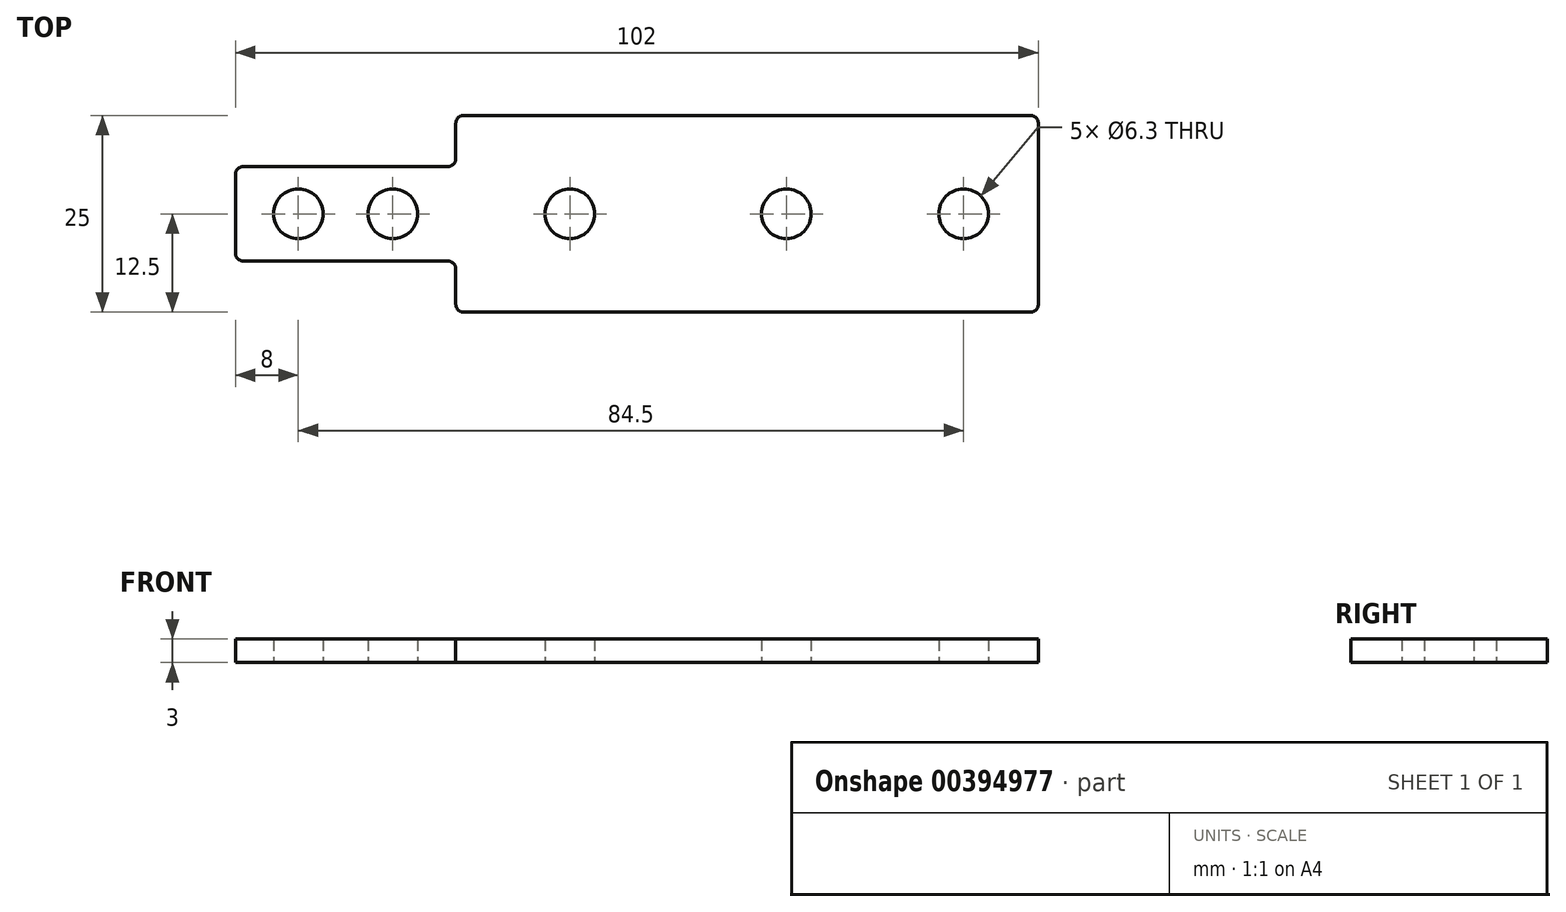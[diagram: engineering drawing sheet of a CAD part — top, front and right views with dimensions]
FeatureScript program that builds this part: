
annotation { "Feature Type Name" : "Feature", "Feature Type Description" : "" }
export const myFeature = defineFeature(function(context is Context, id is Id, definition is map)
    precondition{}
    {
        {
            var Q0;
            Q0=qCreatedBy(makeId("Top.planeOp"),FACE);
            var sketch = newSketch(context, id + "F0", { "sketchPlane" : qUnion([Q0])});
            skLineSegment(sketch, "E0.bottom", {"start": v(0, 12.5) * mm, "end": v(74, 12.5) * mm});
            skLineSegment(sketch, "E0.top", {"start": v(0, -12.5) * mm, "end": v(74, -12.5) * mm});
            skLineSegment(sketch, "E0.left", {"start": v(0, 12.5) * mm, "end": v(0, -12.5) * mm});
            skLineSegment(sketch, "E0.right", {"start": v(74, 12.5) * mm, "end": v(74, -12.5) * mm});
            skLineSegment(sketch, "E1.bottom", {"start": v(0, 6) * mm, "end": v(-28, 6) * mm});
            skLineSegment(sketch, "E1.top", {"start": v(0, -6) * mm, "end": v(-28, -6) * mm});
            skLineSegment(sketch, "E1.left", {"start": v(0, 6) * mm, "end": v(0, -6) * mm});
            skLineSegment(sketch, "E1.right", {"start": v(-28, 6) * mm, "end": v(-28, -6) * mm});
            skLineSegment(sketch, "E2", {"start": v(-28, 0) * mm, "end": v(74, 0) * mm, "construction": true});
            skCircle(sketch, "E3", {"center": v(14.5, 0) * mm, "radius": 3.15 * mm});
            skCircle(sketch, "E4", {"center": v(42, 0) * mm, "radius": 3.15 * mm});
            skCircle(sketch, "E5", {"center": v(64.5, 0) * mm, "radius": 3.15 * mm});
            skCircle(sketch, "E6", {"center": v(-20, 0) * mm, "radius": 3.15 * mm});
            skCircle(sketch, "E7", {"center": v(-8, 0) * mm, "radius": 3.15 * mm});
            skSolve(sketch);
        }
        {
            var Q0;
            Q0 = qSketchRegion(id + "F0", true);
            extrude(context, id + "F1", {"entities" : qUnion([Q0]), "depth" : 3 * mm});
        }
        {
            var Q0;
            Q0=makeQuery(id+"F1.opExtrude","SWEPT_EDGE",EDGE,{"disambiguationData":[OSD([sQuery(id+"F0.wireOp",EDGE,"E1.bottom"),sQuery(id+"F0.wireOp",EDGE,"E1.right")])]});
            var Q1;
            Q1=makeQuery(id+"F1.opExtrude","SWEPT_EDGE",EDGE,{"disambiguationData":[OSD([sQuery(id+"F0.wireOp",EDGE,"E1.top"),sQuery(id+"F0.wireOp",EDGE,"E1.right")])]});
            var Q2;
            Q2=makeQuery(id+"F1.opExtrude","SWEPT_EDGE",EDGE,{"disambiguationData":[OSD([sQuery(id+"F0.wireOp",EDGE,"E0.left"),sQuery(id+"F0.wireOp",EDGE,"E1.bottom"),sQuery(id+"F0.wireOp",EDGE,"E1.left")])]});
            var Q3;
            Q3=makeQuery(id+"F1.opExtrude","SWEPT_EDGE",EDGE,{"disambiguationData":[OSD([sQuery(id+"F0.wireOp",EDGE,"E0.bottom"),sQuery(id+"F0.wireOp",EDGE,"E0.left")])]});
            var Q4;
            Q4=makeQuery(id+"F1.opExtrude","SWEPT_EDGE",EDGE,{"disambiguationData":[OSD([sQuery(id+"F0.wireOp",EDGE,"E0.left"),sQuery(id+"F0.wireOp",EDGE,"E1.top"),sQuery(id+"F0.wireOp",EDGE,"E1.left")])]});
            var Q5;
            Q5=makeQuery(id+"F1.opExtrude","SWEPT_EDGE",EDGE,{"disambiguationData":[OSD([sQuery(id+"F0.wireOp",EDGE,"E0.top"),sQuery(id+"F0.wireOp",EDGE,"E0.left")])]});
            var Q6;
            Q6=makeQuery(id+"F1.opExtrude","SWEPT_EDGE",EDGE,{"disambiguationData":[OSD([sQuery(id+"F0.wireOp",EDGE,"E0.top"),sQuery(id+"F0.wireOp",EDGE,"E0.right")])]});
            var Q7;
            Q7=makeQuery(id+"F1.opExtrude","SWEPT_EDGE",EDGE,{"disambiguationData":[OSD([sQuery(id+"F0.wireOp",EDGE,"E0.bottom"),sQuery(id+"F0.wireOp",EDGE,"E0.right")])]});
            fillet(context, id + "F2", {"entities" : qUnion([Q0, Q1, Q2, Q3, Q4, Q5, Q6, Q7]), "radius" : 1 * mm, "tangentPropagation" : true, "allowEdgeOverflow" : false});
        }
    });
